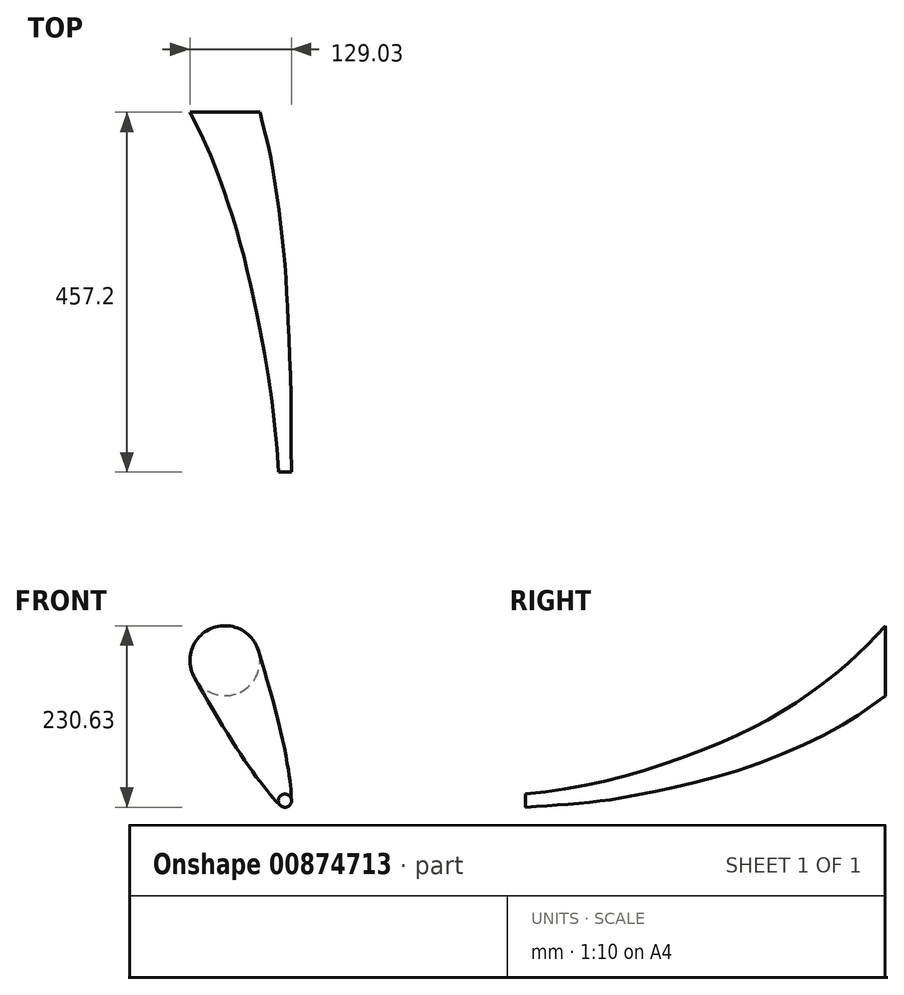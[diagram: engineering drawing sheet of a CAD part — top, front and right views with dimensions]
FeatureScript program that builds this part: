
annotation { "Feature Type Name" : "Feature", "Feature Type Description" : "" }
export const myFeature = defineFeature(function(context is Context, id is Id, definition is map)
    precondition{}
    {
        {
            var Q0;
            Q0=qCreatedBy(makeId("Front.planeOp"),FACE);
            var sketch = newSketch(context, id + "F0", { "sketchPlane" : qUnion([Q0])});
            skCircle(sketch, "E0", {"center": v(0, 0) * mm, "radius": 8.38 * mm});
            skSolve(sketch);
        }
        {
            var Q0;
            Q0=qCreatedBy(makeId("Right.planeOp"),FACE);
            var sketch = newSketch(context, id + "F1", { "sketchPlane" : qUnion([Q0])});
            skLineSegment(sketch, "E1", {"start": v(0, 0) * mm, "end": v(457.2, 0) * mm});
            skLineSegment(sketch, "E2", {"start": v(457.2, 0) * mm, "end": v(457.2, 177.8) * mm});
            skSolve(sketch);
        }
        {
            var Q0;
            Q0=qCreatedBy(makeId("Front.planeOp"),FACE);
            cPlane(context, id + "F2", {"entities" : qUnion([Q0]), "cplaneType" : CPlaneType.OFFSET, "offset" : 457.2 * mm, "oppositeDirection" : true, "width" : 152.4 * mm, "height" : 152.4 * mm});
        }
        {
            var Q0;
            Q0=qCreatedBy(id+"F2.planeOp",FACE);
            var sketch = newSketch(context, id + "F3", { "sketchPlane" : qUnion([Q0])});
            skLineSegment(sketch, "E3", {"start": v(0, 177.8) * mm, "end": v(-76.2, 177.8) * mm});
            skSolve(sketch);
        }
        {
            var Q0;
            Q0=qCreatedBy(id+"F2.planeOp",FACE);
            var sketch = newSketch(context, id + "F4", { "sketchPlane" : qUnion([Q0])});
            skCircle(sketch, "E4", {"center": v(-76.2, 177.8) * mm, "radius": 44.45 * mm});
            skSolve(sketch);
        }
        {
            var Q0;
            Q0=sQuery(id+"F3.wireOp",VERTEX,"E3.end");
            var Q1;
            Q1=sQuery(id+"F1.wireOp",VERTEX,"E1.start");
            var Q2;
            Q2=sQuery(id+"F1.wireOp",VERTEX,"E1.end");
            cPlane(context, id + "F5", {"entities" : qUnion([Q0, Q1, Q2]), "cplaneType" : CPlaneType.THREE_POINT, "offset" : 25.4 * mm, "width" : 152.4 * mm, "height" : 152.4 * mm});
        }
        {
            var Q0;
            Q0=qCreatedBy(id+"F5.planeOp",FACE);
            var sketch = newSketch(context, id + "F6", { "sketchPlane" : qUnion([Q0])});
            skFitSpline(sketch, "E5", {"points": [v(0, 0) * mm, v(-159.43, 28.64) * mm, v(-297.8, 79.67) * mm, v(-405.32, 146.53) * mm, v(-457.2, 193.44) * mm], "startDerivative": vector(-466.6, 0) * mm, "endDerivative": vector(-236.96, 228.99) * mm});
            skSolve(sketch);
        }
        {
            var Q0;
            Q0=sQuery(id+"F6.wireOp",EDGE,"E5");
            var Q1;
            Q1=sQuery(id+"F0.wireOp",EDGE,"E0");
            var Q2;
            Q2=sQuery(id+"F4.wireOp",EDGE,"E4");
            loft(context, id + "F7", {"bodyType" : ToolBodyType.SURFACE, "addSections" : true, "spine" : qUnion([Q0]), "sectionCount" : 5, "wireProfilesArray" : [{ "wireProfileEntities" : qUnion([Q1]) }, { "wireProfileEntities" : qUnion([Q2]) }]});
        }
    });
